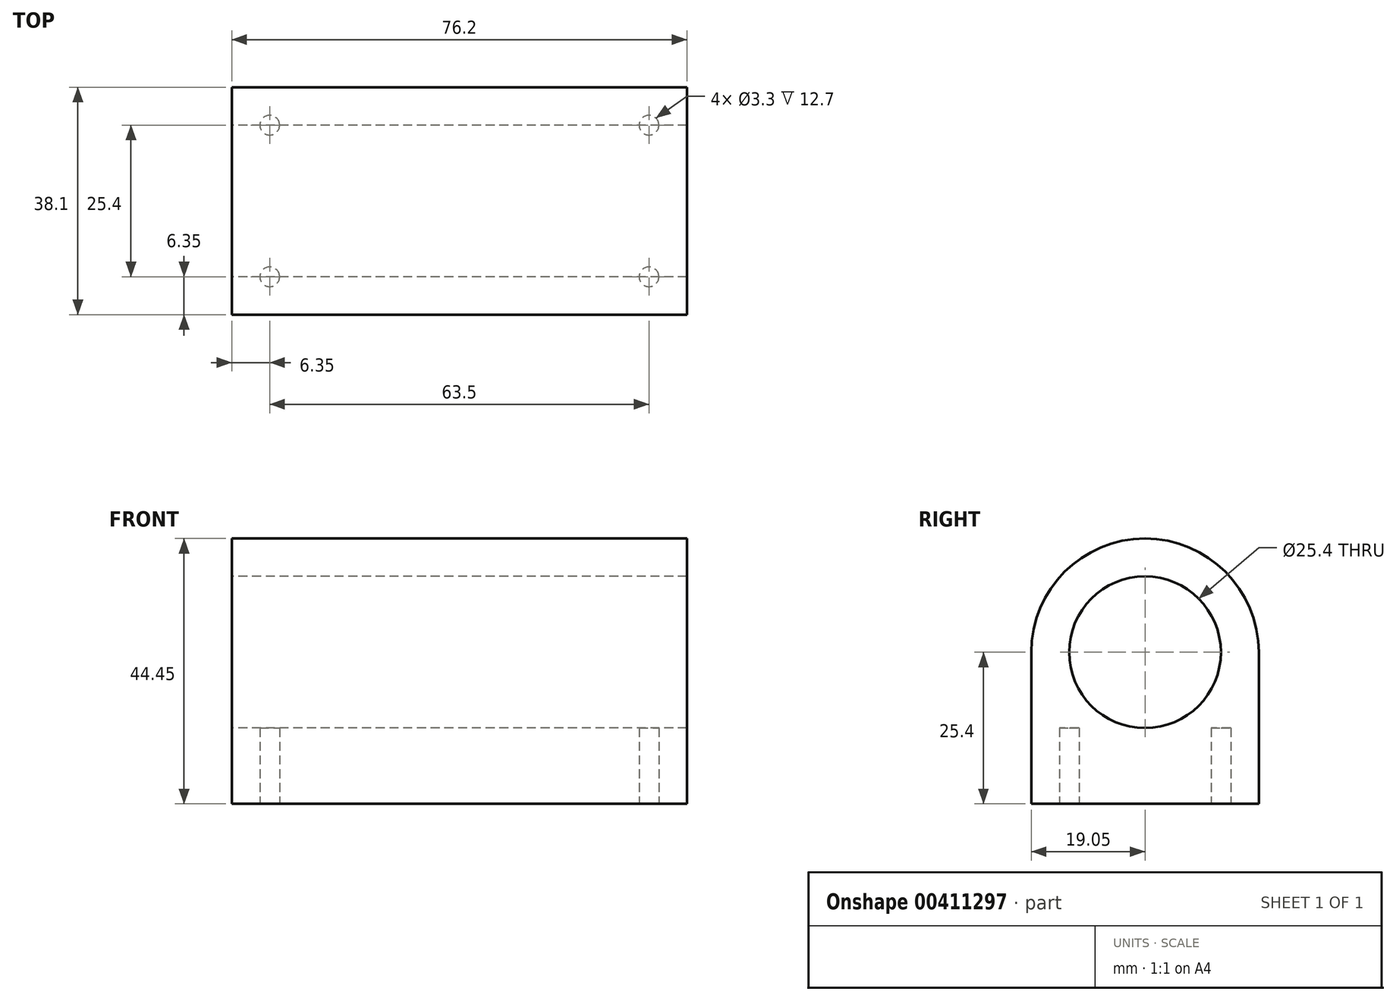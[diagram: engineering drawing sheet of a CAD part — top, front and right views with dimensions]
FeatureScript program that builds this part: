
annotation { "Feature Type Name" : "Feature", "Feature Type Description" : "" }
export const myFeature = defineFeature(function(context is Context, id is Id, definition is map)
    precondition{}
    {
        {
            var Q0;
            Q0=qCreatedBy(makeId("Right.planeOp"),FACE);
            var sketch = newSketch(context, id + "F0", { "sketchPlane" : qUnion([Q0])});
            skLineSegment(sketch, "E0", {"start": v(-19.05, 0) * mm, "end": v(-19.05, -25.4) * mm});
            skLineSegment(sketch, "E1", {"start": v(-19.05, -25.4) * mm, "end": v(19.05, -25.4) * mm});
            skLineSegment(sketch, "E2", {"start": v(19.05, -25.4) * mm, "end": v(19.05, 0) * mm});
            skArc(sketch, "E3", {"start": v(19.05, 0) * mm, "mid": v(0, 19.05) * mm, "end": v(-19.05, 0) * mm});
            skCircle(sketch, "E4", {"center": v(0, 0) * mm, "radius": 12.7 * mm});
            skSolve(sketch);
        }
        {
            var Q0;
            Q0 = qSketchRegion(id + "F0", true);
            extrude(context, id + "F1", {"entities" : qUnion([Q0]), "endBound" : BoundingType.SYMMETRIC, "depth" : 76.2 * mm});
        }
        {
            var Q0;
            Q0=makeQuery(id+"F1.opExtrude","SWEPT_FACE",FACE,{"disambiguationData":[OSD([sQuery(id+"F0.wireOp",EDGE,"E1")])]});
            var sketch = newSketch(context, id + "F2", { "sketchPlane" : qUnion([Q0])});
            skCircle(sketch, "E5", {"center": v(-31.75, 12.7) * mm, "radius": 1.65 * mm});
            skCircle(sketch, "E6", {"center": v(-31.75, -12.7) * mm, "radius": 1.65 * mm});
            skCircle(sketch, "E7", {"center": v(31.75, 12.7) * mm, "radius": 1.65 * mm});
            skCircle(sketch, "E8", {"center": v(31.75, -12.7) * mm, "radius": 1.65 * mm});
            skSolve(sketch);
        }
        {
            var Q0;
            Q0 = qSketchRegion(id + "F2", true);
            extrude(context, id + "F3", {"entities" : qUnion([Q0]), "operationType" : NewBodyOperationType.REMOVE, "oppositeDirection" : true, "depth" : 12.7 * mm});
        }
    });
